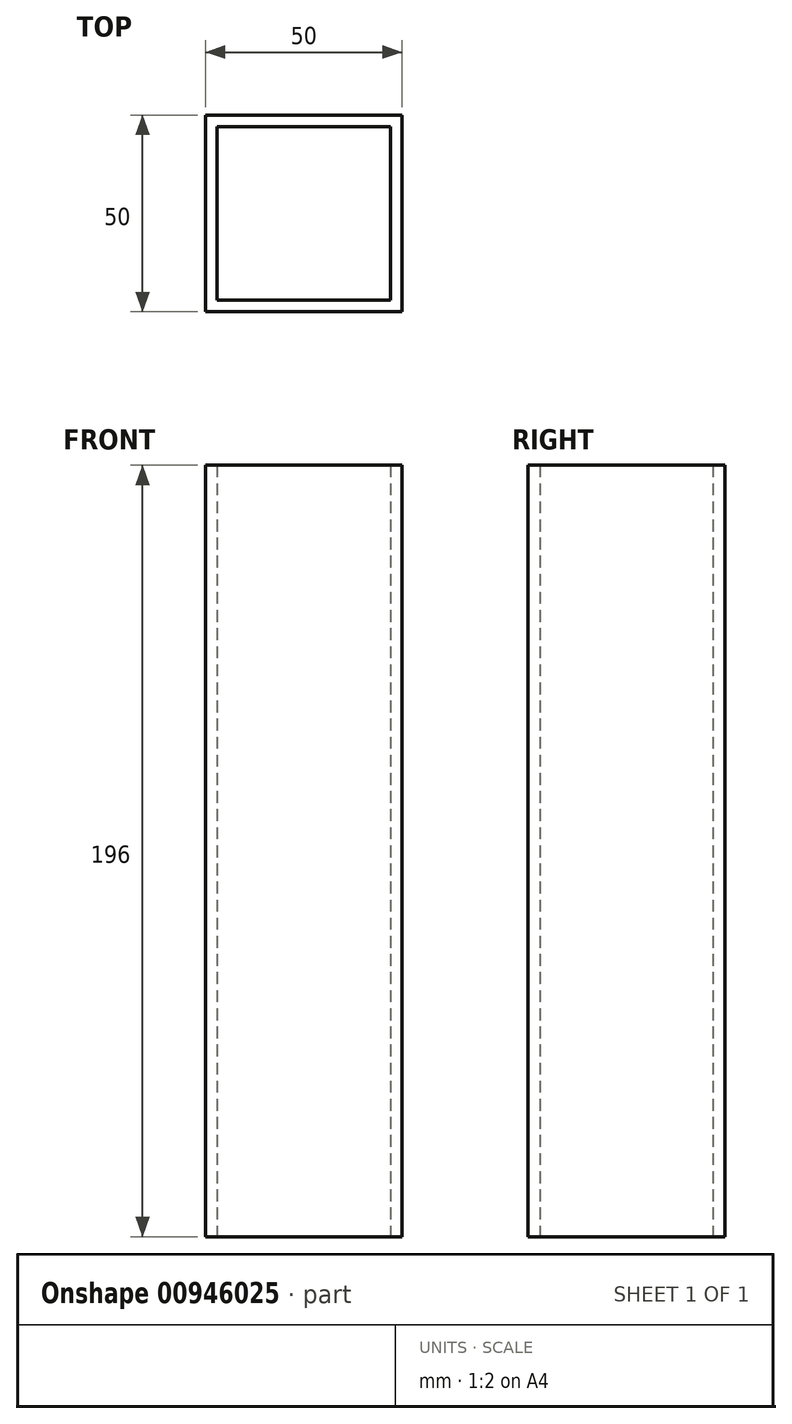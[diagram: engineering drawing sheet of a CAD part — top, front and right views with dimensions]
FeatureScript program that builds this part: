
annotation { "Feature Type Name" : "Feature", "Feature Type Description" : "" }
export const myFeature = defineFeature(function(context is Context, id is Id, definition is map)
    precondition{}
    {
        {
            var Q0;
            Q0=qCreatedBy(makeId("Top.planeOp"),FACE);
            var sketch = newSketch(context, id + "F0", { "sketchPlane" : qUnion([Q0])});
            skLineSegment(sketch, "E0.bottom", {"start": v(25, 25) * mm, "end": v(-25, 25) * mm});
            skLineSegment(sketch, "E0.top", {"start": v(25, -25) * mm, "end": v(-25, -25) * mm});
            skLineSegment(sketch, "E0.left", {"start": v(25, 25) * mm, "end": v(25, -25) * mm});
            skLineSegment(sketch, "E0.right", {"start": v(-25, 25) * mm, "end": v(-25, -25) * mm});
            skPoint(sketch, "E0.middle", {"position": v(0, 0) * mm});
            skLineSegment(sketch, "E1.0", {"start": v(22, -22) * mm, "end": v(-22, -22) * mm});
            skLineSegment(sketch, "E1.1", {"start": v(22, 22) * mm, "end": v(22, -22) * mm});
            skLineSegment(sketch, "E1.2", {"start": v(22, 22) * mm, "end": v(-22, 22) * mm});
            skLineSegment(sketch, "E1.3", {"start": v(-22, 22) * mm, "end": v(-22, -22) * mm});
            skSolve(sketch);
        }
        {
            var Q0;
            Q0=qCreatedBy(makeId("Top.planeOp"),FACE);
            cPlane(context, id + "F1", {"entities" : qUnion([Q0]), "cplaneType" : CPlaneType.OFFSET, "offset" : 196 * mm, "width" : 150 * mm, "height" : 150 * mm});
        }
        {
            var Q0;
            Q0=makeQuery(id+"F0.imprint","IMPRINT",FACE,{"disambiguationData":[TD([[makeQuery(id+"F0.imprint","IMPRINT",EDGE,{"derivedFrom":sQuery(id+"F0.wireOp",EDGE,"E0.bottom")}),1.0]])]});
            var Q1;
            Q1=qCreatedBy(id+"F1.planeOp",FACE);
            extrude(context, id + "F2", {"entities" : qUnion([Q0]), "endBound" : BoundingType.UP_TO_SURFACE, "depth" : 25 * mm, "endBoundEntityFace" : qUnion([Q1]), "offsetDistance" : 25 * mm});
        }
    });
